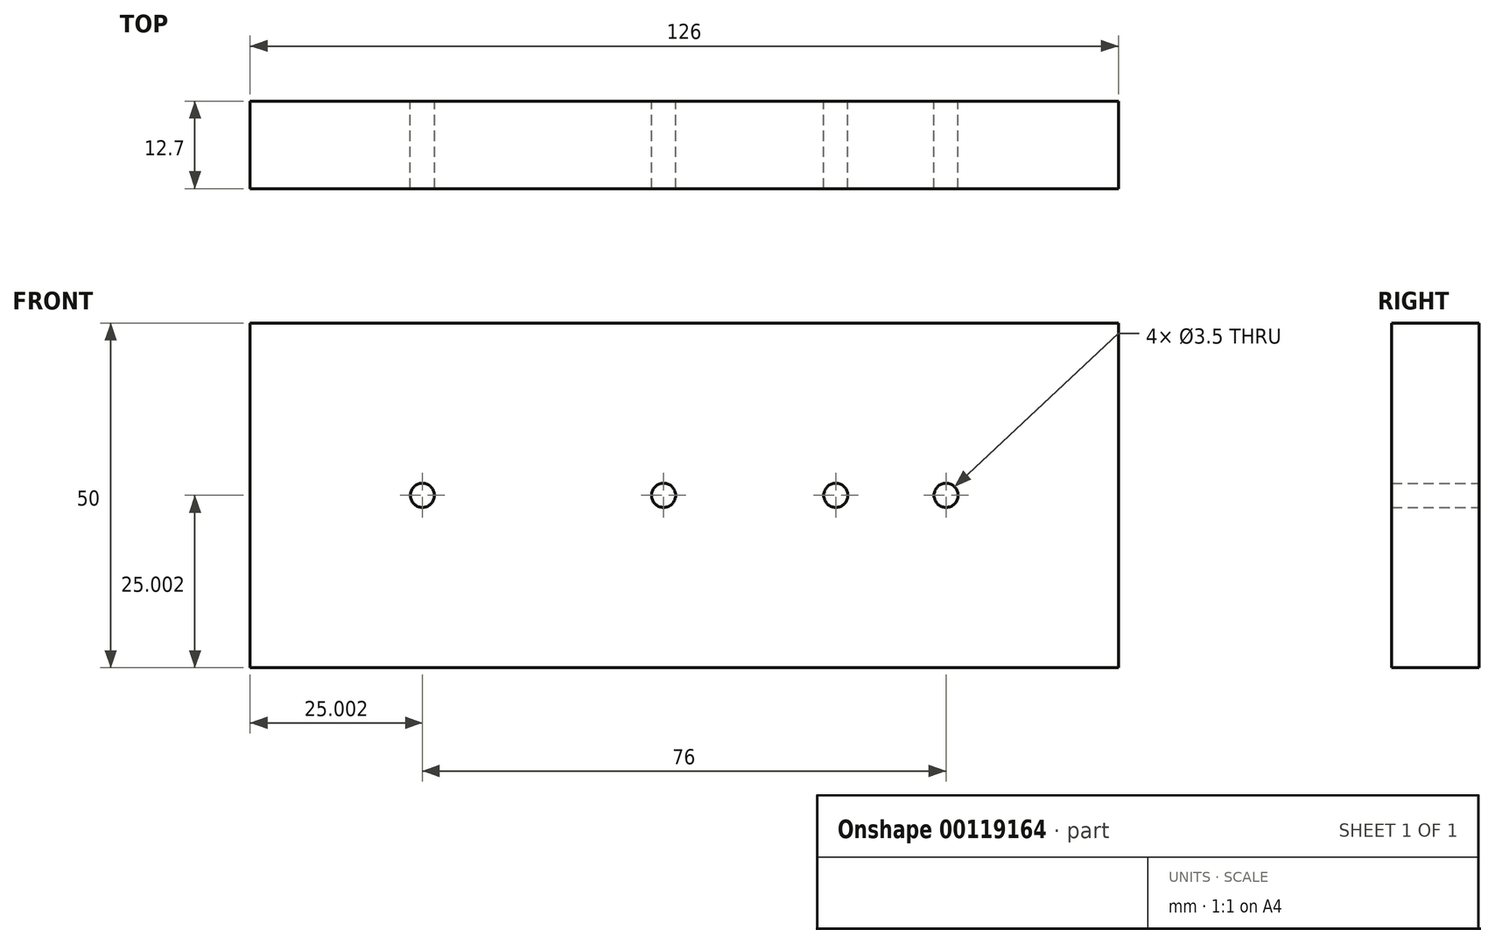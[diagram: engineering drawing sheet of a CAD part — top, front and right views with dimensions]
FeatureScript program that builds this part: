
annotation { "Feature Type Name" : "Feature", "Feature Type Description" : "" }
export const myFeature = defineFeature(function(context is Context, id is Id, definition is map)
    precondition{}
    {
        {
            var Q0;
            Q0=qCreatedBy(makeId("Front.planeOp"),FACE);
            var sketch = newSketch(context, id + "F0", { "sketchPlane" : qUnion([Q0])});
            skCircle(sketch, "E0", {"center": v(-40.7, 9.53) * mm, "radius": 1.75 * mm});
            skCircle(sketch, "E1.1.0.0", {"center": v(-5.7, 9.53) * mm, "radius": 1.75 * mm});
            skCircle(sketch, "E1.2.0.0", {"center": v(19.3, 9.53) * mm, "radius": 1.75 * mm});
            skCircle(sketch, "E2.0.3.0", {"center": v(35.3, 9.53) * mm, "radius": 1.75 * mm});
            skLineSegment(sketch, "E3", {"start": v(-40.7, 9.53) * mm, "end": v(-5.7, 9.53) * mm});
            skLineSegment(sketch, "E4", {"start": v(-5.7, 9.53) * mm, "end": v(19.3, 9.53) * mm});
            skLineSegment(sketch, "E5", {"start": v(19.3, 9.53) * mm, "end": v(35.3, 9.53) * mm});
            skLineSegment(sketch, "E6.bottom", {"start": v(-65.7, -15.47) * mm, "end": v(60.3, -15.47) * mm});
            skLineSegment(sketch, "E6.left", {"start": v(-65.7, -15.47) * mm, "end": v(-65.7, 34.53) * mm});
            skLineSegment(sketch, "E6.right", {"start": v(60.3, -15.47) * mm, "end": v(60.3, 34.53) * mm});
            skLineSegment(sketch, "E7", {"start": v(-65.7, 34.53) * mm, "end": v(60.3, 34.53) * mm});
            skSolve(sketch);
        }
        {
            var Q0;
            Q0=makeQuery(id+"F0.imprint","IMPRINT",FACE,{"disambiguationData":[TD([[makeQuery(id+"F0.imprint","IMPRINT",EDGE,{"derivedFrom":sQuery(id+"F0.wireOp",EDGE,"E0")}),-1.0]])]});
            extrude(context, id + "F1", {"entities" : qUnion([Q0]), "depth" : 12.7 * mm});
        }
    });
